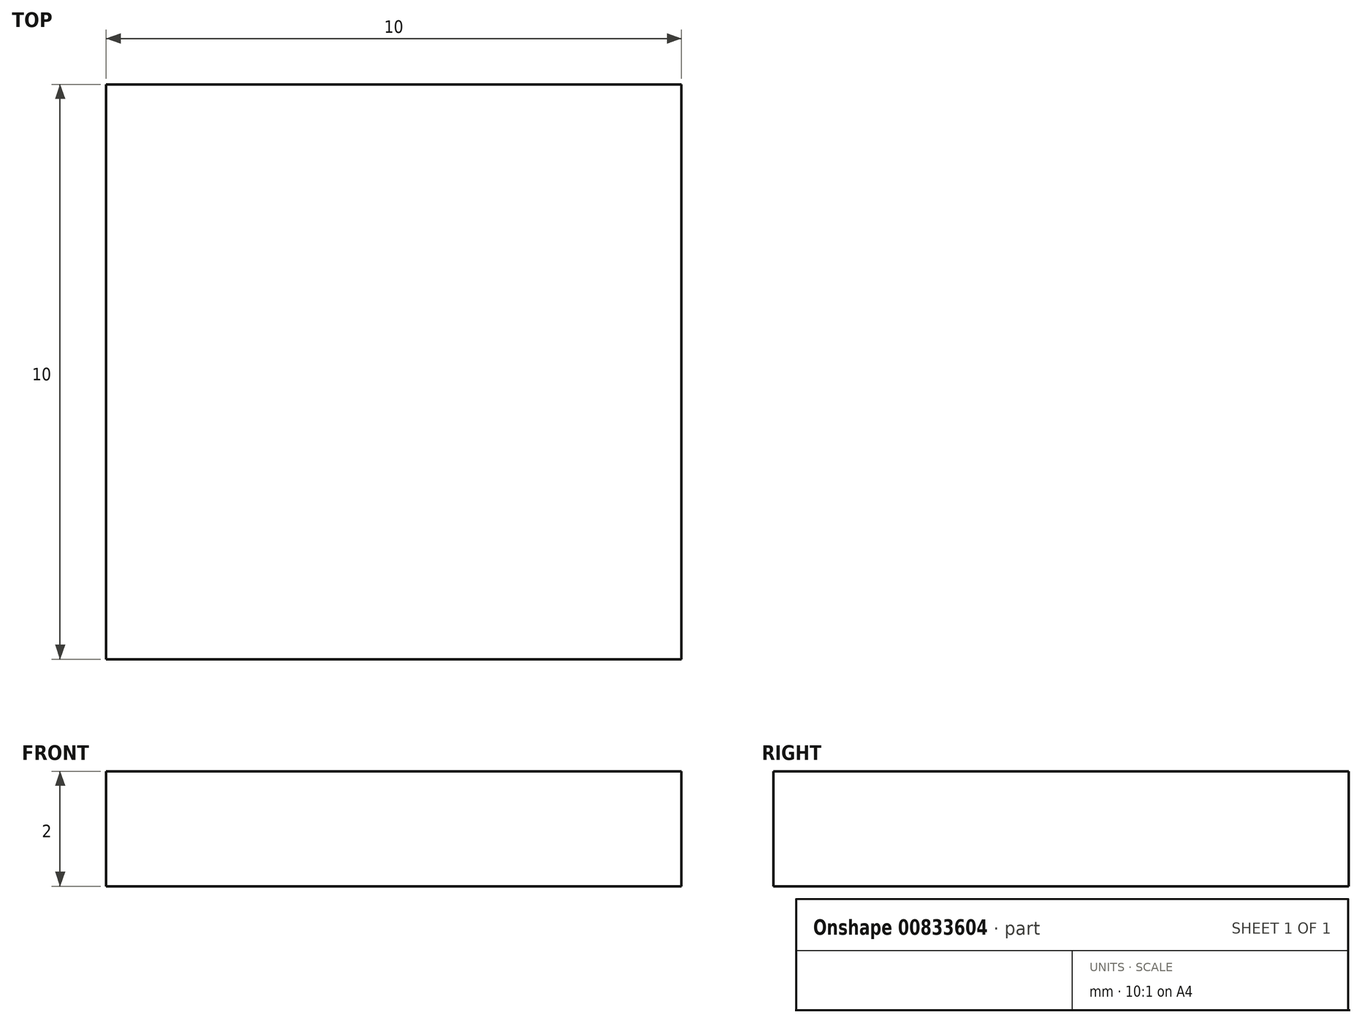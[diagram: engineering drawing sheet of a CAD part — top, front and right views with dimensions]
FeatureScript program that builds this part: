
annotation { "Feature Type Name" : "Feature", "Feature Type Description" : "" }
export const myFeature = defineFeature(function(context is Context, id is Id, definition is map)
    precondition{}
    {
        {
            var Q0;
            Q0=qCreatedBy(makeId("Top.planeOp"),FACE);
            var sketch = newSketch(context, id + "F0", { "sketchPlane" : qUnion([Q0])});
            skLineSegment(sketch, "E0.bottom", {"start": v(5, -5) * mm, "end": v(-5, -5) * mm});
            skLineSegment(sketch, "E0.top", {"start": v(5, 5) * mm, "end": v(-5, 5) * mm});
            skLineSegment(sketch, "E0.left", {"start": v(5, -5) * mm, "end": v(5, 5) * mm});
            skLineSegment(sketch, "E0.right", {"start": v(-5, -5) * mm, "end": v(-5, 5) * mm});
            skPoint(sketch, "E0.middle", {"position": v(0, 0) * mm});
            skSolve(sketch);
        }
        {
            var Q0;
            Q0=makeQuery(id+"F0.imprint","IMPRINT",FACE,{"disambiguationData":[TD([[makeQuery(id+"F0.imprint","IMPRINT",EDGE,{"derivedFrom":sQuery(id+"F0.wireOp",EDGE,"E0.bottom")}),-1.0]])]});
            extrude(context, id + "F1", {"entities" : qUnion([Q0]), "depth" : 2 * mm, "offsetDistance" : 25 * mm});
        }
    });
